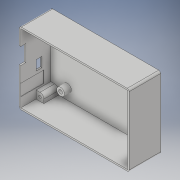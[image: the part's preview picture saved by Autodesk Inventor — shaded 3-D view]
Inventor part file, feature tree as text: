
AUTODESK INVENTOR PART (.ipt)
format: ipt  version: 2019 (Build 230136000, 136)  size: 443,392 bytes
history: native  units: mm
features: other x9, extrude x7, hole x2, fillet x1
ambient origin geometry x8: Origin, YZ Plane, XZ Plane, XY Plane, X Axis, Y Axis, Z Axis, Center Point
bodies: Solid1 (feature_tree)
feature tree (19):
  extrude  "Extrusion1"  Depth=109.0mm
  extrude  "Extrusion2"  Depth=70.0mm
  other  "stena_RJ45"
  other  "srouby_upevneni"
  extrude  "Extrusion3"  Depth=1.2mm TaperAngle=0.0deg
  extrude  "Extrusion4"  Depth=8.0mm
  extrude  "Extrusion5"  Depth=17.0mm
  hole  "Hole1"  [1 undecoded]
  hole  "Hole2"  [1 undecoded]
  extrude  "Extrusion7"  Depth=74.9mm
  extrude  "Extrusion8"  Depth=8.0mm
  fillet  "Fillet1"  Radius=82.0mm
  other  "zaklad"
  other  "uchyt_pro_desku"
  other  "steny"
  other  "diry"
  other  "uchyt_pro_desku_diry"
  other  "dira_USB"
  other  "vyrez_napajeci_jack_nepouzivany"
note: 2 required parameter values undecoded (feature->parameter linkage not recoverable at this tier; creation-order binding heuristic only, values carry confidence <= 0.55)
